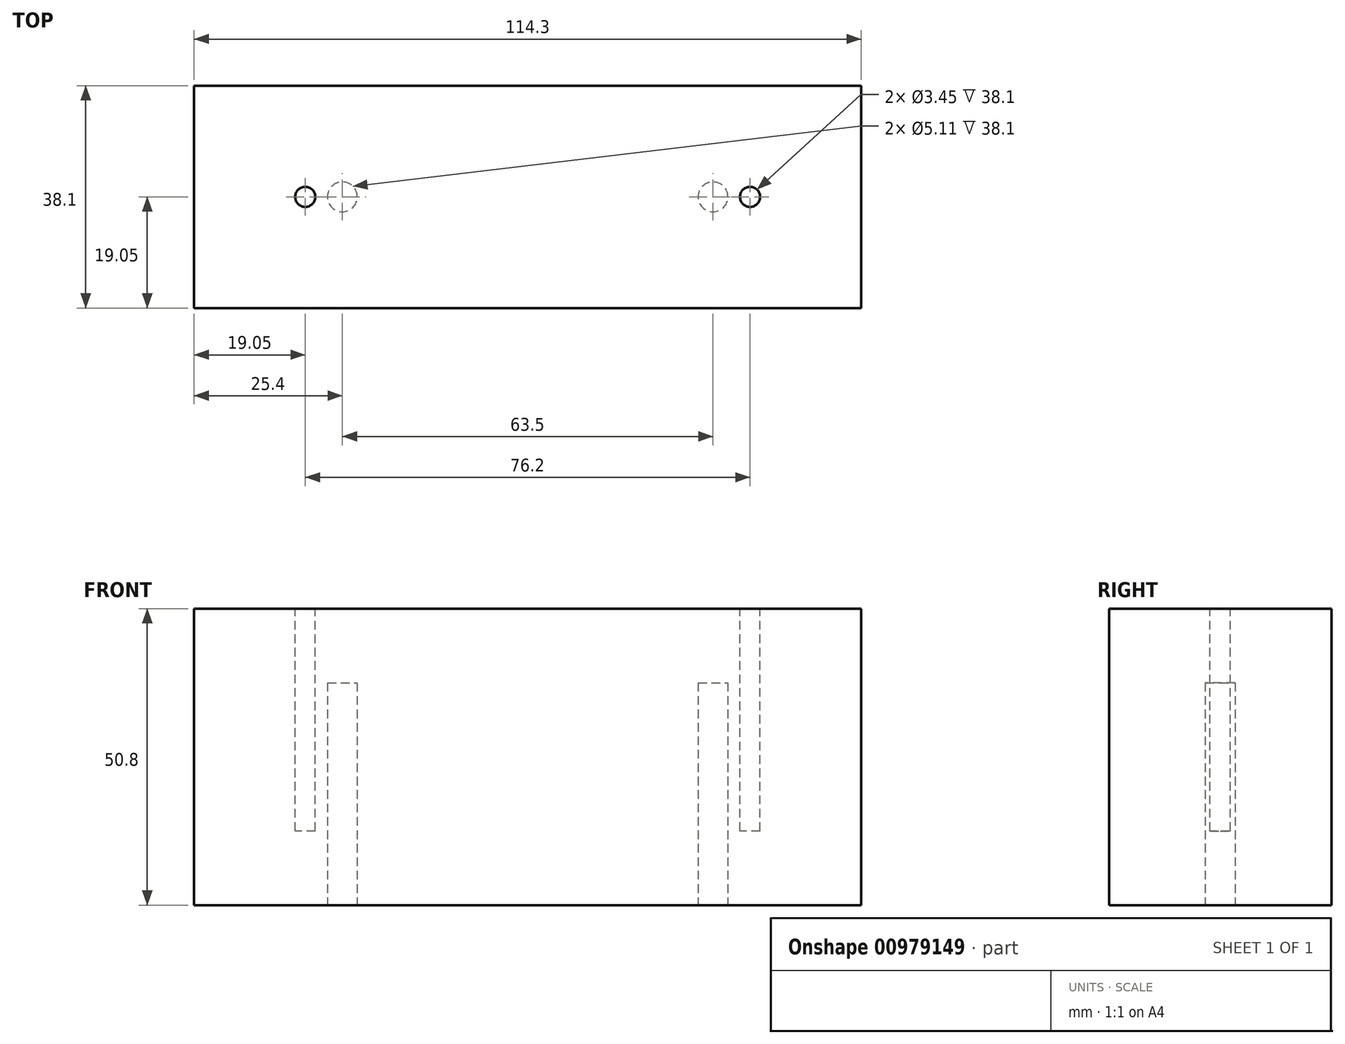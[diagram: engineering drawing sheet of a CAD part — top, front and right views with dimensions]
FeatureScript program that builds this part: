
annotation { "Feature Type Name" : "Feature", "Feature Type Description" : "" }
export const myFeature = defineFeature(function(context is Context, id is Id, definition is map)
    precondition{}
    {
        {
            var Q0;
            Q0=qCreatedBy(makeId("Top.planeOp"),FACE);
            var sketch = newSketch(context, id + "F0", { "sketchPlane" : qUnion([Q0])});
            skLineSegment(sketch, "E0.bottom", {"start": v(57.15, -19.05) * mm, "end": v(-57.15, -19.05) * mm});
            skLineSegment(sketch, "E0.top", {"start": v(57.15, 19.05) * mm, "end": v(-57.15, 19.05) * mm});
            skLineSegment(sketch, "E0.left", {"start": v(57.15, -19.05) * mm, "end": v(57.15, 19.05) * mm});
            skLineSegment(sketch, "E0.right", {"start": v(-57.15, -19.05) * mm, "end": v(-57.15, 19.05) * mm});
            skPoint(sketch, "E0.middle", {"position": v(0, 0) * mm});
            skSolve(sketch);
        }
        {
            var Q0;
            Q0=makeQuery(id+"F0.imprint","IMPRINT",FACE,{"disambiguationData":[TD([[makeQuery(id+"F0.imprint","IMPRINT",EDGE,{"derivedFrom":sQuery(id+"F0.wireOp",EDGE,"E0.bottom")}),-1.0]])]});
            extrude(context, id + "F1", {"entities" : qUnion([Q0]), "depth" : 50.8 * mm, "offsetDistance" : 25.4 * mm});
        }
        {
            var Q0;
            Q0=makeQuery(id+"F1.opExtrude","CAP_FACE",FACE,{"disambiguationData":[OSD([sQuery(id+"F0.wireOp",EDGE,"E0.bottom"),sQuery(id+"F0.wireOp",EDGE,"E0.top"),sQuery(id+"F0.wireOp",EDGE,"E0.left"),sQuery(id+"F0.wireOp",EDGE,"E0.right")])],"isStart":false});
            var sketch = newSketch(context, id + "F2", { "sketchPlane" : qUnion([Q0])});
            skLineSegment(sketch, "E1", {"start": v(-52.57, 0) * mm, "end": v(51.27, 0) * mm, "construction": true});
            skCircle(sketch, "E2", {"center": v(-38.1, 0) * mm, "radius": 1.73 * mm});
            skCircle(sketch, "E3", {"center": v(38.1, 0) * mm, "radius": 1.73 * mm});
            skSolve(sketch);
        }
        {
            var Q0;
            Q0 = qSketchRegion(id + "F2", true);
            extrude(context, id + "F3", {"entities" : qUnion([Q0]), "operationType" : NewBodyOperationType.REMOVE, "oppositeDirection" : true, "depth" : 38.1 * mm, "offsetDistance" : 25.4 * mm});
        }
        {
            var Q0;
            Q0=makeQuery(id+"F1.opExtrude","CAP_FACE",FACE,{"disambiguationData":[OSD([sQuery(id+"F0.wireOp",EDGE,"E0.bottom"),sQuery(id+"F0.wireOp",EDGE,"E0.top"),sQuery(id+"F0.wireOp",EDGE,"E0.left"),sQuery(id+"F0.wireOp",EDGE,"E0.right")])],"isStart":true});
            var sketch = newSketch(context, id + "F4", { "sketchPlane" : qUnion([Q0])});
            skLineSegment(sketch, "E4", {"start": v(-47.7, 0) * mm, "end": v(51.44, 0) * mm, "construction": true});
            skCircle(sketch, "E5", {"center": v(-31.75, 0) * mm, "radius": 2.55 * mm});
            skCircle(sketch, "E6", {"center": v(31.75, 0) * mm, "radius": 2.55 * mm});
            skSolve(sketch);
        }
        {
            var Q0;
            Q0 = qSketchRegion(id + "F4", true);
            extrude(context, id + "F5", {"entities" : qUnion([Q0]), "operationType" : NewBodyOperationType.REMOVE, "oppositeDirection" : true, "depth" : 38.1 * mm, "offsetDistance" : 25.4 * mm});
        }
    });
